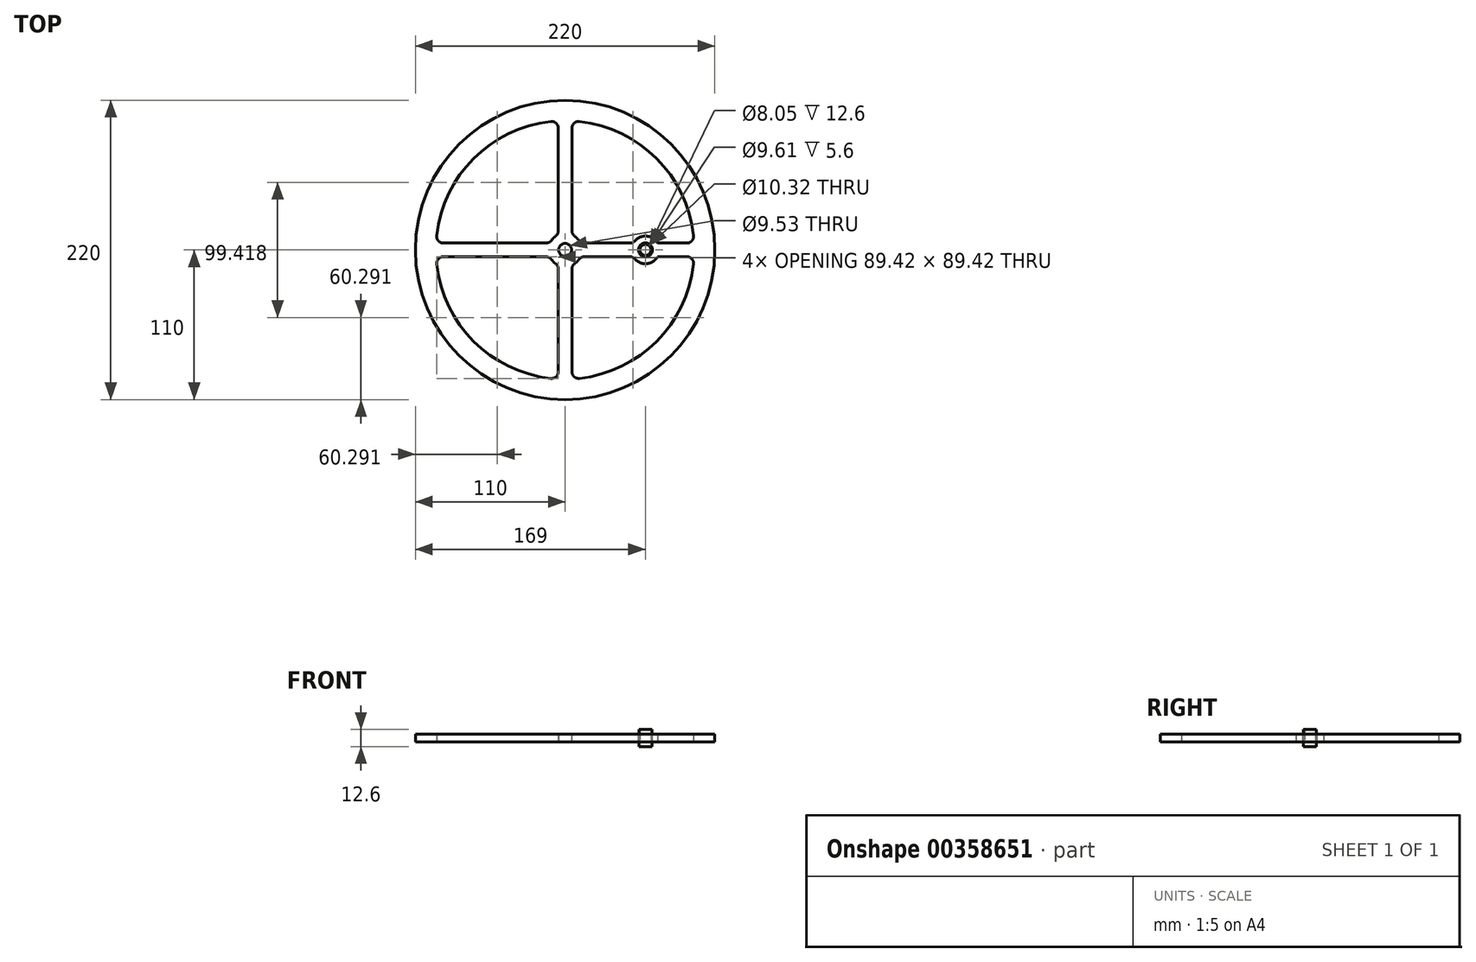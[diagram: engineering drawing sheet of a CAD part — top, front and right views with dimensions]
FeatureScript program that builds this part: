
annotation { "Feature Type Name" : "Feature", "Feature Type Description" : "" }
export const myFeature = defineFeature(function(context is Context, id is Id, definition is map)
    precondition{}
    {
        {
            var Q0;
            Q0=qCreatedBy(makeId("Top.planeOp"),FACE);
            var sketch = newSketch(context, id + "F0", { "sketchPlane" : qUnion([Q0])});
            skCircle(sketch, "E0", {"center": v(0, 0) * mm, "radius": 4.76 * mm});
            skArc(sketch, "E1", {"start": v(10, 7.1) * mm, "mid": v(7.77, 9.48) * mm, "end": v(5, 11.2) * mm});
            skCircle(sketch, "E2", {"center": v(59, 0) * mm, "radius": 5.16 * mm});
            skLineSegment(sketch, "E3", {"start": v(0, 0) * mm, "end": v(59, 0) * mm, "construction": true});
            skLineSegment(sketch, "E4", {"start": v(14.07, -5) * mm, "end": v(47.6, -5) * mm});
            skArc(sketch, "E5", {"start": v(14.07, -5) * mm, "mid": v(11.78, -5.56) * mm, "end": v(10, -7.1) * mm});
            skLineSegment(sketch, "E6.trimOffspring", {"start": v(14.07, 5) * mm, "end": v(47.6, 5) * mm});
            skArc(sketch, "E7", {"start": v(10, 7.1) * mm, "mid": v(11.78, 5.56) * mm, "end": v(14.07, 5) * mm});
            skArc(sketch, "E8", {"start": v(51.36, -6.7) * mm, "mid": v(60.04, -10.1) * mm, "end": v(67.84, -5) * mm});
            skArc(sketch, "E9", {"start": v(47.6, 5) * mm, "mid": v(49.67, 5.45) * mm, "end": v(51.36, 6.7) * mm});
            skArc(sketch, "E10", {"start": v(51.36, -6.7) * mm, "mid": v(49.67, -5.45) * mm, "end": v(47.6, -5) * mm});
            skCircle(sketch, "E11", {"center": v(0, 0) * mm, "radius": 110 * mm});
            skArc(sketch, "E12", {"start": v(-94.87, -5) * mm, "mid": v(-67.18, -67.18) * mm, "end": v(-5, -94.87) * mm});
            skLineSegment(sketch, "E13", {"start": v(0, 95) * mm, "end": v(0, -95) * mm, "construction": true});
            skLineSegment(sketch, "E14", {"start": v(-95, 0) * mm, "end": v(0, 0) * mm, "construction": true});
            skLineSegment(sketch, "E15", {"start": v(-5, 94.87) * mm, "end": v(-5, 11.2) * mm});
            skLineSegment(sketch, "E16", {"start": v(5, 94.87) * mm, "end": v(5, 11.2) * mm});
            skLineSegment(sketch, "E17", {"start": v(-94.87, 5) * mm, "end": v(-11.2, 5) * mm});
            skLineSegment(sketch, "E18", {"start": v(-94.87, -5) * mm, "end": v(-11.2, -5) * mm});
            skLineSegment(sketch, "E19", {"start": v(-5, -11.2) * mm, "end": v(-5, -94.87) * mm});
            skLineSegment(sketch, "E20", {"start": v(5, -11.2) * mm, "end": v(5, -94.87) * mm});
            skLineSegment(sketch, "E21", {"start": v(67.84, 5) * mm, "end": v(94.87, 5) * mm});
            skLineSegment(sketch, "E22", {"start": v(67.84, -5) * mm, "end": v(94.87, -5) * mm});
            skArc(sketch, "E23.trimOffspring", {"start": v(-5, 94.87) * mm, "mid": v(-67.18, 67.18) * mm, "end": v(-94.87, 5) * mm});
            skArc(sketch, "E24.trimOffspring", {"start": v(-11.2, -5) * mm, "mid": v(-8.67, -8.67) * mm, "end": v(-5, -11.2) * mm});
            skArc(sketch, "E25.trimOffspring", {"start": v(-5, 11.2) * mm, "mid": v(-8.67, 8.67) * mm, "end": v(-11.2, 5) * mm});
            skArc(sketch, "E26.trimOffspring", {"start": v(5, -11.2) * mm, "mid": v(7.77, -9.48) * mm, "end": v(10, -7.1) * mm});
            skArc(sketch, "E27.trimOffspring", {"start": v(5, -94.87) * mm, "mid": v(67.18, -67.18) * mm, "end": v(94.87, -5) * mm});
            skArc(sketch, "E28.trimOffspring", {"start": v(67.84, 5) * mm, "mid": v(60.04, 10.1) * mm, "end": v(51.36, 6.7) * mm});
            skArc(sketch, "E29.trimOffspring", {"start": v(94.87, 5) * mm, "mid": v(67.18, 67.18) * mm, "end": v(5, 94.87) * mm});
            skSolve(sketch);
        }
        {
            var Q0;
            Q0=makeQuery(id+"F0.imprint","IMPRINT",FACE,{"disambiguationData":[TD([[makeQuery(id+"F0.imprint","IMPRINT",EDGE,{"derivedFrom":sQuery(id+"F0.wireOp",EDGE,"E0")}),-1.0]])]});
            extrude(context, id + "F1", {"entities" : qUnion([Q0]), "depth" : 5.6 * mm, "offsetDistance" : 25 * mm});
        }
        {
            var Q0;
            Q0=makeQuery(id+"F1.opExtrude","CAP_FACE",FACE,{"disambiguationData":[OSD([sQuery(id+"F0.wireOp",EDGE,"E0"),sQuery(id+"F0.wireOp",EDGE,"E1"),sQuery(id+"F0.wireOp",EDGE,"E2"),sQuery(id+"F0.wireOp",EDGE,"E4"),sQuery(id+"F0.wireOp",EDGE,"E5"),sQuery(id+"F0.wireOp",EDGE,"E6.trimOffspring"),sQuery(id+"F0.wireOp",EDGE,"E7"),sQuery(id+"F0.wireOp",EDGE,"E8"),sQuery(id+"F0.wireOp",EDGE,"E9"),sQuery(id+"F0.wireOp",EDGE,"E10")])],"isStart":false});
            var sketch = newSketch(context, id + "F2", { "sketchPlane" : qUnion([Q0])});
            skCircle(sketch, "E30", {"center": v(59, 0) * mm, "radius": 5.16 * mm});
            skCircle(sketch, "E31", {"center": v(59, 0) * mm, "radius": 4.8 * mm});
            skSolve(sketch);
        }
        {
            var Q0;
            Q0=qSketchRegion(id+"F2",true);
            extrude(context, id + "F3", {"entities" : qUnion([Q0]), "depth" : 0 * mm, "offsetDistance" : 25 * mm, "hasSecondDirection" : true, "secondDirectionOppositeDirection" : true, "secondDirectionDepth" : 5.6 * mm});
        }
        {
            var Q0;
            Q0=makeQuery(id+"F1.opExtrude","CAP_FACE",FACE,{"disambiguationData":[OSD([sQuery(id+"F0.wireOp",EDGE,"E0"),sQuery(id+"F0.wireOp",EDGE,"E1"),sQuery(id+"F0.wireOp",EDGE,"E2"),sQuery(id+"F0.wireOp",EDGE,"E4"),sQuery(id+"F0.wireOp",EDGE,"E5"),sQuery(id+"F0.wireOp",EDGE,"E6.trimOffspring"),sQuery(id+"F0.wireOp",EDGE,"E7"),sQuery(id+"F0.wireOp",EDGE,"E8"),sQuery(id+"F0.wireOp",EDGE,"E9"),sQuery(id+"F0.wireOp",EDGE,"E10")])],"isStart":false});
            var sketch = newSketch(context, id + "F4", { "sketchPlane" : qUnion([Q0])});
            skCircle(sketch, "E32", {"center": v(59, 0) * mm, "radius": 4.76 * mm});
            skCircle(sketch, "E33", {"center": v(59, 0) * mm, "radius": 4.03 * mm});
            skSolve(sketch);
        }
        {
            var Q0;
            Q0=qSketchRegion(id+"F4",true);
            extrude(context, id + "F5", {"entities" : qUnion([Q0]), "depth" : 3.5 * mm, "offsetDistance" : 25 * mm, "hasSecondDirection" : true, "secondDirectionOppositeDirection" : true, "secondDirectionDepth" : (5.6 + 3.5) * mm});
        }
        {
            var Q0;
            Q0=makeQuery(id+"F1.opExtrude","SWEPT_EDGE",EDGE,{"disambiguationData":[OSD([sQuery(id+"F0.wireOp",EDGE,"E20"),sQuery(id+"F0.wireOp",EDGE,"E26.trimOffspring")])]});
            var Q1;
            Q1=makeQuery(id+"F1.opExtrude","SWEPT_EDGE",EDGE,{"disambiguationData":[OSD([sQuery(id+"F0.wireOp",EDGE,"E19"),sQuery(id+"F0.wireOp",EDGE,"E24.trimOffspring")])]});
            var Q2;
            Q2=makeQuery(id+"F1.opExtrude","SWEPT_EDGE",EDGE,{"disambiguationData":[OSD([sQuery(id+"F0.wireOp",EDGE,"E18"),sQuery(id+"F0.wireOp",EDGE,"E24.trimOffspring")])]});
            var Q3;
            Q3=makeQuery(id+"F1.opExtrude","SWEPT_EDGE",EDGE,{"disambiguationData":[OSD([sQuery(id+"F0.wireOp",EDGE,"E17"),sQuery(id+"F0.wireOp",EDGE,"E25.trimOffspring")])]});
            var Q4;
            Q4=makeQuery(id+"F1.opExtrude","SWEPT_EDGE",EDGE,{"disambiguationData":[OSD([sQuery(id+"F0.wireOp",EDGE,"E15"),sQuery(id+"F0.wireOp",EDGE,"E25.trimOffspring")])]});
            var Q5;
            Q5=makeQuery(id+"F1.opExtrude","SWEPT_EDGE",EDGE,{"disambiguationData":[OSD([sQuery(id+"F0.wireOp",EDGE,"E1"),sQuery(id+"F0.wireOp",EDGE,"E16")])]});
            var Q6;
            Q6=makeQuery(id+"F1.opExtrude","SWEPT_EDGE",EDGE,{"disambiguationData":[OSD([sQuery(id+"F0.wireOp",EDGE,"E20"),sQuery(id+"F0.wireOp",EDGE,"E27.trimOffspring")])]});
            var Q7;
            Q7=makeQuery(id+"F1.opExtrude","SWEPT_EDGE",EDGE,{"disambiguationData":[OSD([sQuery(id+"F0.wireOp",EDGE,"E12"),sQuery(id+"F0.wireOp",EDGE,"E19")])]});
            var Q8;
            Q8=makeQuery(id+"F1.opExtrude","SWEPT_EDGE",EDGE,{"disambiguationData":[OSD([sQuery(id+"F0.wireOp",EDGE,"E12"),sQuery(id+"F0.wireOp",EDGE,"E18")])]});
            var Q9;
            Q9=makeQuery(id+"F1.opExtrude","SWEPT_EDGE",EDGE,{"disambiguationData":[OSD([sQuery(id+"F0.wireOp",EDGE,"E17"),sQuery(id+"F0.wireOp",EDGE,"E23.trimOffspring")])]});
            var Q10;
            Q10=makeQuery(id+"F1.opExtrude","SWEPT_EDGE",EDGE,{"disambiguationData":[OSD([sQuery(id+"F0.wireOp",EDGE,"E16"),sQuery(id+"F0.wireOp",EDGE,"E29.trimOffspring")])]});
            var Q11;
            Q11=makeQuery(id+"F1.opExtrude","SWEPT_EDGE",EDGE,{"disambiguationData":[OSD([sQuery(id+"F0.wireOp",EDGE,"E15"),sQuery(id+"F0.wireOp",EDGE,"E23.trimOffspring")])]});
            var Q12;
            Q12=makeQuery(id+"F1.opExtrude","SWEPT_EDGE",EDGE,{"disambiguationData":[OSD([sQuery(id+"F0.wireOp",EDGE,"E21"),sQuery(id+"F0.wireOp",EDGE,"E29.trimOffspring")])]});
            var Q13;
            Q13=makeQuery(id+"F1.opExtrude","SWEPT_EDGE",EDGE,{"disambiguationData":[OSD([sQuery(id+"F0.wireOp",EDGE,"E22"),sQuery(id+"F0.wireOp",EDGE,"E27.trimOffspring")])]});
            fillet(context, id + "F6", {"entities" : qUnion([Q0, Q1, Q2, Q3, Q4, Q5, Q6, Q7, Q8, Q9, Q10, Q11, Q12, Q13]), "radius" : 5 * mm, "tangentPropagation" : true, "allowEdgeOverflow" : false});
        }
    });
